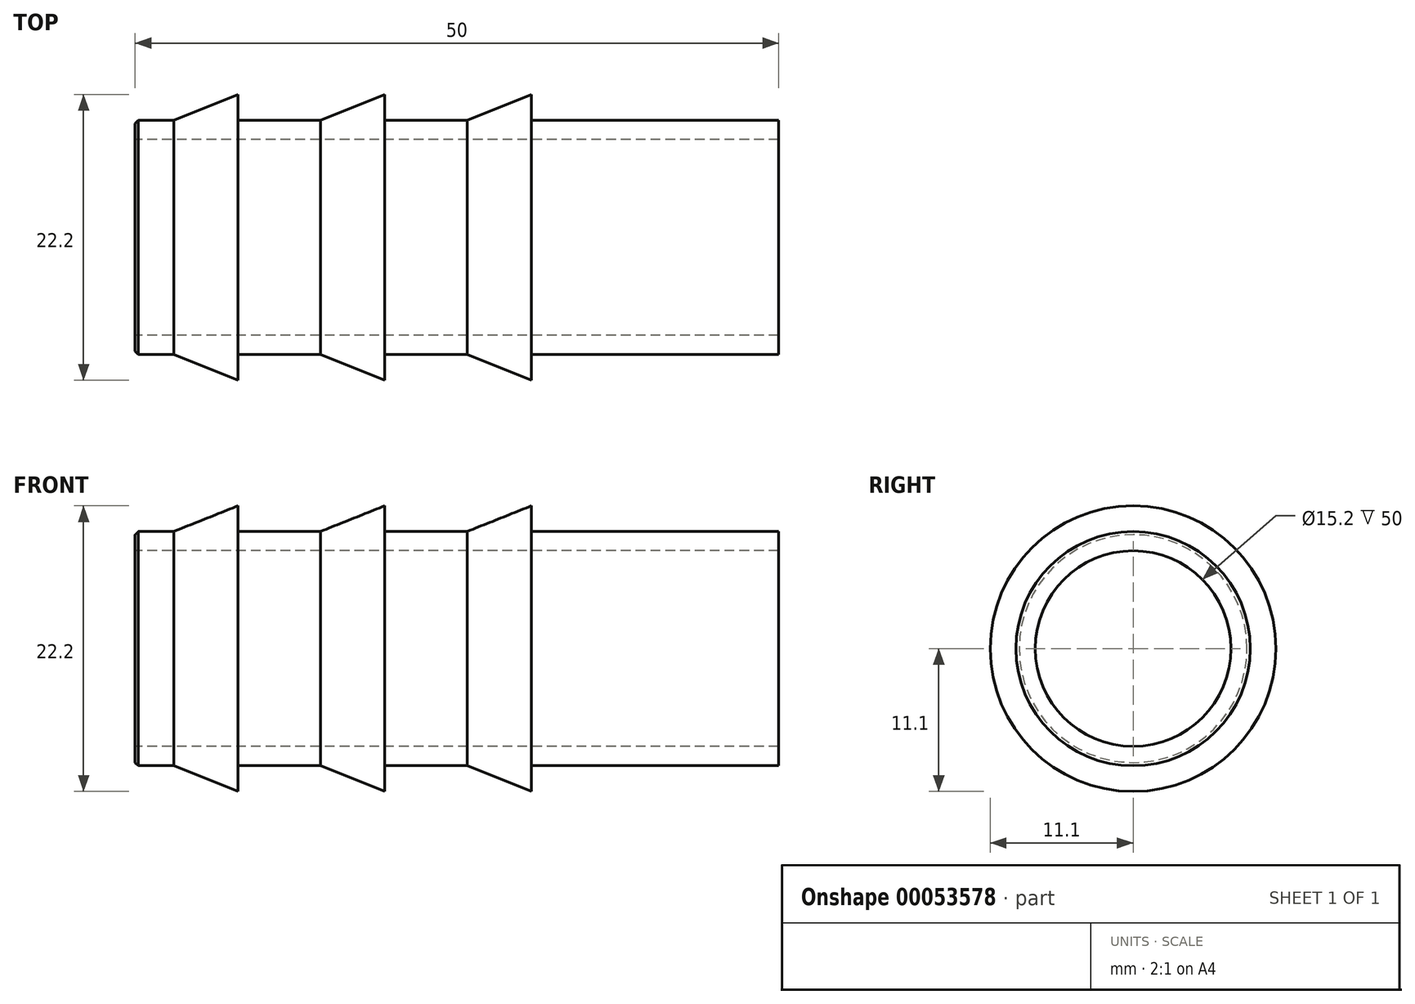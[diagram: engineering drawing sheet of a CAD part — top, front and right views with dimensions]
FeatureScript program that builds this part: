
annotation { "Feature Type Name" : "Feature", "Feature Type Description" : "" }
export const myFeature = defineFeature(function(context is Context, id is Id, definition is map)
    precondition{}
    {
        {
            var Q0;
            Q0=qCreatedBy(makeId("Front.planeOp"),FACE);
            var sketch = newSketch(context, id + "F0", { "sketchPlane" : qUnion([Q0])});
            skLineSegment(sketch, "E0", {"start": v(-20.92, 0) * mm, "end": v(23.77, 0) * mm, "construction": true});
            skLineSegment(sketch, "E1", {"start": v(0, 7.6) * mm, "end": v(50, 7.6) * mm});
            skLineSegment(sketch, "E2", {"start": v(0, 7.6) * mm, "end": v(0, 9.1) * mm});
            skLineSegment(sketch, "E3", {"start": v(0, 9.1) * mm, "end": v(3, 9.1) * mm});
            skLineSegment(sketch, "E4", {"start": v(3, 9.1) * mm, "end": v(8, 11.1) * mm});
            skLineSegment(sketch, "E5", {"start": v(8, 11.1) * mm, "end": v(8, 9.1) * mm});
            skLineSegment(sketch, "E6", {"start": v(8, 9.1) * mm, "end": v(14.4, 9.1) * mm});
            skLineSegment(sketch, "E7", {"start": v(14.4, 9.1) * mm, "end": v(19.4, 11.1) * mm});
            skLineSegment(sketch, "E8", {"start": v(19.4, 11.1) * mm, "end": v(19.4, 9.1) * mm});
            skLineSegment(sketch, "E9", {"start": v(19.4, 9.1) * mm, "end": v(25.8, 9.1) * mm});
            skLineSegment(sketch, "E10", {"start": v(25.8, 9.1) * mm, "end": v(30.8, 11.1) * mm});
            skLineSegment(sketch, "E11", {"start": v(30.8, 11.1) * mm, "end": v(30.8, 9.1) * mm});
            skLineSegment(sketch, "E12", {"start": v(30.8, 9.1) * mm, "end": v(50, 9.1) * mm});
            skLineSegment(sketch, "E13", {"start": v(50, 9.1) * mm, "end": v(50, 7.6) * mm});
            skSolve(sketch);
        }
        {
            var Q0;
            Q0=makeQuery(id+"F0.imprint","IMPRINT",FACE,{"disambiguationData":[TD([[makeQuery(id+"F0.imprint","IMPRINT",EDGE,{"derivedFrom":sQuery(id+"F0.wireOp",EDGE,"E1")}),1.0]])]});
            var Q1;
            Q1=sQuery(id+"F0.wireOp",EDGE,"E0");
            revolve(context, id + "F1", {"entities" : qUnion([Q0]), "axis" : qUnion([Q1]), "revolveType" : RevolveType.FULL});
        }
        {
            var Q0;
            Q0=makeQuery(id+"F1.opRevolve","SWEPT_EDGE",EDGE,{"disambiguationData":[OSD([sQuery(id+"F0.wireOp",EDGE,"E2"),sQuery(id+"F0.wireOp",EDGE,"E3")])]});
            chamfer(context, id + "F2", {"entities" : qUnion([Q0]), "width" : 0.25 * mm, "tangentPropagation" : true});
        }
    });
